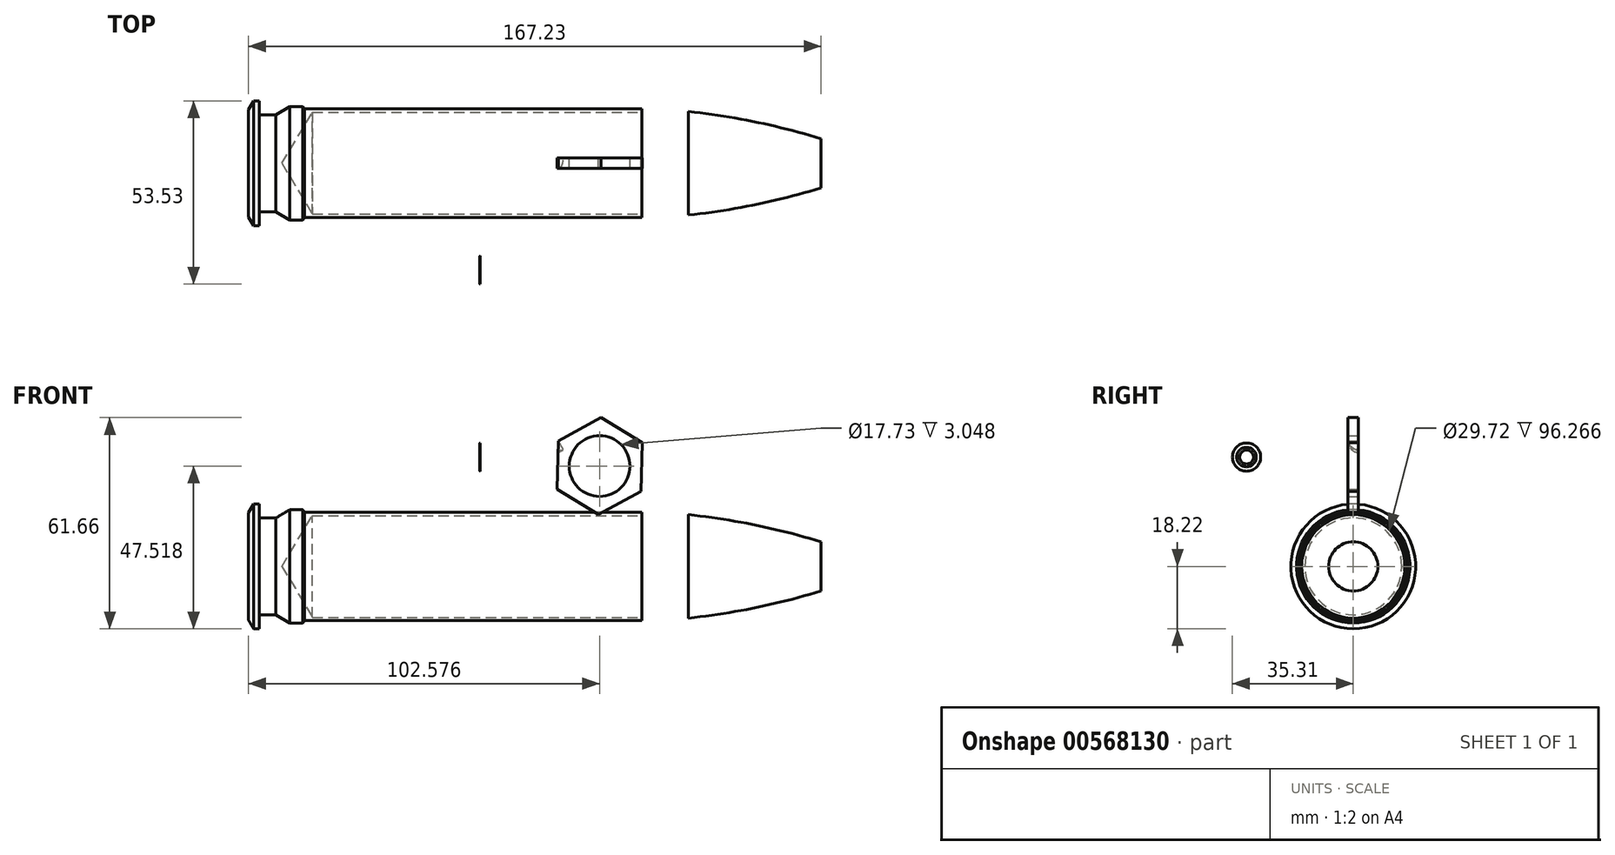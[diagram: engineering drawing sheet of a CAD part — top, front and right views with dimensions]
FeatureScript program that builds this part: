
annotation { "Feature Type Name" : "Feature", "Feature Type Description" : "" }
export const myFeature = defineFeature(function(context is Context, id is Id, definition is map)
    precondition{}
    {
        {
            var Q0;
            Q0=qCreatedBy(makeId("Front.planeOp"),FACE);
            var sketch = newSketch(context, id + "F0", { "sketchPlane" : qUnion([Q0])});
            skLineSegment(sketch, "E0", {"start": v(-51.8, -16.56) * mm, "end": v(-51.19, -15.92) * mm});
            skLineSegment(sketch, "E1", {"start": v(-51.19, -15.92) * mm, "end": v(47.36, -15.92) * mm});
            skLineSegment(sketch, "E2", {"start": v(-51.19, 15.87) * mm, "end": v(-51.75, 16.55) * mm});
            skLineSegment(sketch, "E3", {"start": v(-55.62, -16.56) * mm, "end": v(-59.6, -14.07) * mm});
            skLineSegment(sketch, "E4", {"start": v(-55.56, 16.55) * mm, "end": v(-59.6, 14.15) * mm});
            skLineSegment(sketch, "E5", {"start": v(-59.6, 14.15) * mm, "end": v(-64.43, 14.15) * mm});
            skLineSegment(sketch, "E6", {"start": v(-59.6, -14.07) * mm, "end": v(-64.43, -14.07) * mm});
            skLineSegment(sketch, "E7", {"start": v(-64.43, -14.07) * mm, "end": v(-64.43, -18.14) * mm});
            skLineSegment(sketch, "E8", {"start": v(-64.43, -18.14) * mm, "end": v(-67.6, -18.14) * mm});
            skLineSegment(sketch, "E9", {"start": v(-64.43, 14.15) * mm, "end": v(-64.43, 18.22) * mm});
            skLineSegment(sketch, "E10", {"start": v(-64.43, 18.22) * mm, "end": v(-67.6, 18.22) * mm});
            skLineSegment(sketch, "E11", {"start": v(-67.6, 18.22) * mm, "end": v(-67.6, -18.14) * mm});
            skLineSegment(sketch, "E12", {"start": v(-51.8, -16.56) * mm, "end": v(-55.62, -16.56) * mm});
            skLineSegment(sketch, "E13", {"start": v(-55.56, 16.55) * mm, "end": v(-51.75, 16.55) * mm});
            skLineSegment(sketch, "E14", {"start": v(-51.19, 15.87) * mm, "end": v(47.36, 15.87) * mm});
            skLineSegment(sketch, "E15", {"start": v(47.36, 15.87) * mm, "end": v(47.36, -15.92) * mm});
            skLineSegment(sketch, "E16", {"start": v(-67.6, 0) * mm, "end": v(47.36, 0) * mm});
            skSolve(sketch);
        }
        {
            var Q0;
            Q0=makeQuery(id+"F0.imprint","IMPRINT",FACE,{"disambiguationData":[TD([[makeQuery(id+"F0.imprint","IMPRINT",EDGE,{"derivedFrom":sQuery(id+"F0.wireOp",EDGE,"E2")}),1.0]])]});
            var Q1;
            Q1=sQuery(id+"F0.wireOp",EDGE,"E16");
            revolve(context, id + "F1", {"entities" : qUnion([Q0]), "axis" : qUnion([Q1]), "revolveType" : RevolveType.FULL});
        }
        {
            var Q0;
            Q0=makeQuery(id+"F1.opRevolve","SWEPT_EDGE",EDGE,{"disambiguationData":[OSD([sQuery(id+"F0.wireOp",EDGE,"E10"),sQuery(id+"F0.wireOp",EDGE,"E11")])]});
            chamfer(context, id + "F2", {"entities" : qUnion([Q0]), "chamferType" : ChamferType.OFFSET_ANGLE, "width" : 2.54 * mm, "oppositeDirection" : false, "angle" : 30 * degree, "tangentPropagation" : true});
        }
        {
            var Q0;
            Q0=makeQuery(id+"F1.opRevolve","SWEPT_FACE",FACE,{"disambiguationData":[OSD([sQuery(id+"F0.wireOp",EDGE,"E15")])]});
            cPlane(context, id + "F3", {"entities" : qUnion([Q0]), "cplaneType" : CPlaneType.OFFSET, "offset" : 0.25 * mm, "width" : 152.4 * mm, "height" : 152.4 * mm});
        }
        {
            var Q0;
            Q0=qCreatedBy(id+"F3.planeOp",FACE);
            var sketch = newSketch(context, id + "F4", { "sketchPlane" : qUnion([Q0])});
            skCircle(sketch, "E17", {"center": v(0, 0) * mm, "radius": 14.86 * mm});
            skSolve(sketch);
        }
        {
            var Q0;
            Q0=sQuery(id+"F4.wireOp",VERTEX,"E17.center");
            var Q1;
            Q1=makeQuery(id+"F1.opRevolve","SWEPT_BODY",BODY,{"disambiguationData":[OSD([sQuery(id+"F0.wireOp",EDGE,"E2"),sQuery(id+"F0.wireOp",EDGE,"E4"),sQuery(id+"F0.wireOp",EDGE,"E5"),sQuery(id+"F0.wireOp",EDGE,"E9"),sQuery(id+"F0.wireOp",EDGE,"E10"),sQuery(id+"F0.wireOp",EDGE,"E11"),sQuery(id+"F0.wireOp",EDGE,"E13"),sQuery(id+"F0.wireOp",EDGE,"E14"),sQuery(id+"F0.wireOp",EDGE,"E15"),sQuery(id+"F0.wireOp",EDGE,"E16")])]});
            hole(context, id + "F5", {"style" : HoleStyle.SIMPLE, "endStyle" : HoleEndStyle.BLIND, "holeDiameter" : 29.72 * mm, "holeDepth" : 96.52 * mm, "isTappedThrough" : true, "tappedDepth" : 12.7 * mm, "tapClearance" : 3, "startFromSketch" : true, "locations" : qUnion([Q0]), "scope" : qUnion([Q1])});
        }
        {
            var Q0;
            Q0=qCreatedBy(makeId("Right.planeOp"),FACE);
            var sketch = newSketch(context, id + "F6", { "sketchPlane" : qUnion([Q0])});
            skCircle(sketch, "E18", {"center": v(-31.18, 31.94) * mm, "radius": 4.13 * mm});
            skCircle(sketch, "E19", {"center": v(-31.18, 31.94) * mm, "radius": 2.86 * mm});
            skCircle(sketch, "E20", {"center": v(-31.18, 31.94) * mm, "radius": 2.03 * mm});
            skSolve(sketch);
        }
        {
            var Q0;
            Q0=makeQuery(id+"F6.imprint","IMPRINT",FACE,{"disambiguationData":[TD([[makeQuery(id+"F6.imprint","IMPRINT",EDGE,{"derivedFrom":sQuery(id+"F6.wireOp",EDGE,"E18")}),1.0]])]});
            var Q1;
            Q1=makeQuery(id+"F6.imprint","IMPRINT",FACE,{"disambiguationData":[TD([[makeQuery(id+"F6.imprint","IMPRINT",EDGE,{"derivedFrom":sQuery(id+"F6.wireOp",EDGE,"E20")}),1.0]])]});
            extrude(context, id + "F7", {"entities" : qUnion([Q0, Q1]), "endBound" : BoundingType.SYMMETRIC, "oppositeDirection" : true, "depth" : 0.2 * mm, "offsetDistance" : 25.4 * mm});
        }
        {
            var Q0;
            Q0=makeQuery(id+"F7.opExtrude","CAP_EDGE",EDGE,{"disambiguationData":[OSD([sQuery(id+"F6.wireOp",EDGE,"E18")])],"isStart":false});
            var Q1;
            Q1=makeQuery(id+"F7.opExtrude","CAP_EDGE",EDGE,{"disambiguationData":[OSD([sQuery(id+"F6.wireOp",EDGE,"E19")])],"isStart":false});
            fillet(context, id + "F8", {"entities" : qUnion([Q0, Q1]), "radius" : 0.2 * mm, "tangentPropagation" : true, "allowEdgeOverflow" : false});
        }
        {
            var Q0;
            Q0=makeQuery(id+"F7.opExtrude","CAP_EDGE",EDGE,{"disambiguationData":[OSD([sQuery(id+"F6.wireOp",EDGE,"E20")])],"isStart":false});
            fillet(context, id + "F9", {"entities" : qUnion([Q0]), "radius" : 1.17 * mm, "tangentPropagation" : true, "rho" : 0.5, "crossSection" : FilletCrossSection.CONIC, "allowEdgeOverflow" : false});
        }
        {
            var Q0;
            Q0=qCreatedBy(makeId("Front.planeOp"),FACE);
            var sketch = newSketch(context, id + "F10", { "sketchPlane" : qUnion([Q0])});
            skLineSegment(sketch, "E21", {"start": v(60.9, 14.72) * mm, "end": v(60.9, -15.12) * mm});
            skLineSegment(sketch, "E22", {"start": v(99.62, 5.52) * mm, "end": v(99.62, -7.18) * mm});
            skArc(sketch, "E23", {"start": v(99.62, 5.52) * mm, "mid": v(80.48, 11.05) * mm, "end": v(60.9, 14.72) * mm});
            skArc(sketch, "E24", {"start": v(60.9, -15.12) * mm, "mid": v(80.45, -12.07) * mm, "end": v(99.62, -7.18) * mm});
            skLineSegment(sketch, "E25", {"start": v(60.9, 0) * mm, "end": v(99.62, 0) * mm});
            skSolve(sketch);
        }
        {
            var Q0;
            {var subQ0=sQuery(id+"F10.wireOp",EDGE,"E24");Q0=makeQuery(id+"F10.imprint","IMPRINT",FACE,{"disambiguationData":[TD([[makeQuery(id+"F10.imprint","IMPRINT",EDGE,{"derivedFrom":subQ0}),1.0]])]});}
            var Q1;
            Q1=sQuery(id+"F10.wireOp",EDGE,"E25");
            revolve(context, id + "F11", {"entities" : qUnion([Q0]), "axis" : qUnion([Q1]), "revolveType" : RevolveType.FULL});
        }
        {
            var Q0;
            Q0=qCreatedBy(makeId("Front.planeOp"),FACE);
            var sketch = newSketch(context, id + "F12", { "sketchPlane" : qUnion([Q0])});
            skCircle(sketch, "E26.cCircle", {"center": v(34.97, 29.3) * mm, "radius": 12.25 * mm, "construction": true});
            skLineSegment(sketch, "E26.0", {"start": v(22.89, 36.67) * mm, "end": v(35.31, 43.44) * mm});
            skLineSegment(sketch, "E26.1", {"start": v(35.31, 43.44) * mm, "end": v(47.39, 36.07) * mm});
            skLineSegment(sketch, "E26.2", {"start": v(47.39, 36.07) * mm, "end": v(47.04, 21.92) * mm});
            skLineSegment(sketch, "E26.3", {"start": v(47.04, 21.92) * mm, "end": v(34.62, 15.15) * mm});
            skLineSegment(sketch, "E26.4", {"start": v(34.62, 15.15) * mm, "end": v(22.54, 22.53) * mm});
            skLineSegment(sketch, "E26.5", {"start": v(22.54, 22.53) * mm, "end": v(22.89, 36.67) * mm});
            skPoint(sketch, "E26.0.midPoint", {"position": v(29.1, 40.06) * mm});
            skCircle(sketch, "E27", {"center": v(34.97, 29.3) * mm, "radius": 8.86 * mm});
            skSolve(sketch);
        }
        {
            var Q0;
            Q0 = qSketchRegion(id + "F12", true);
            extrude(context, id + "F13", {"entities" : qUnion([Q0]), "endBound" : BoundingType.SYMMETRIC, "depth" : 3.05 * mm, "offsetDistance" : 25.4 * mm});
        }
        {
            var Q0;
            Q0 = qSketchRegion(id + "F12", true);
            extrude(context, id + "F14", {"entities" : qUnion([Q0]), "depth" : 3.05 * mm, "offsetDistance" : 25.4 * mm});
        }
        {
            var Q0;
            Q0=makeQuery(id+"F14.opExtrude","SWEPT_BODY",BODY,{"disambiguationData":[OSD([sQuery(id+"F12.wireOp",EDGE,"E26.0"),sQuery(id+"F12.wireOp",EDGE,"E26.1"),sQuery(id+"F12.wireOp",EDGE,"E26.2"),sQuery(id+"F12.wireOp",EDGE,"E26.3"),sQuery(id+"F12.wireOp",EDGE,"E26.4"),sQuery(id+"F12.wireOp",EDGE,"E26.5"),sQuery(id+"F12.wireOp",EDGE,"E27")])]});
            deleteBodies(context, id + "F15", {"entities" : qUnion([Q0])});
        }
        {
            var Q0;
            Q0=makeQuery(id+"F13.opExtrude","SWEPT_FACE",FACE,{"disambiguationData":[OSD([sQuery(id+"F12.wireOp",EDGE,"E26.0")])]});
            var sketch = newSketch(context, id + "F16", { "sketchPlane" : qUnion([Q0])});
            skLineSegment(sketch, "E28", {"start": v(51.8, -1.52) * mm, "end": v(51.8, 1.52) * mm, "construction": true});
            skLineSegment(sketch, "E29", {"start": v(51.8, 1.52) * mm, "end": v(51.8, 0) * mm, "construction": true});
            skLineSegment(sketch, "E30", {"start": v(51.8, 0) * mm, "end": v(37.65, 0) * mm, "construction": true});
            skLineSegment(sketch, "E31", {"start": v(37.65, -1.52) * mm, "end": v(35.48, -0.4) * mm});
            skLineSegment(sketch, "E32", {"start": v(35.48, -0.4) * mm, "end": v(35.48, -1.52) * mm});
            skLineSegment(sketch, "E33", {"start": v(35.48, -1.52) * mm, "end": v(37.65, -1.52) * mm});
            skLineSegment(sketch, "E34.MirrorCS", {"start": v(35.48, 1.52) * mm, "end": v(37.65, 1.52) * mm});
            skLineSegment(sketch, "E35.MirrorCS", {"start": v(37.65, 1.52) * mm, "end": v(35.48, 0.4) * mm});
            skLineSegment(sketch, "E36.MirrorCS", {"start": v(35.48, 0.4) * mm, "end": v(35.48, 1.52) * mm});
            skSolve(sketch);
        }
        {
            var Q0;
            Q0 = qSketchRegion(id + "F16", true);
            var Q1;
            Q1=sQuery(id+"F16.wireOp",EDGE,"E32");
            var Q2;
            Q2=sQuery(id+"F16.wireOp",EDGE,"E33");
            var Q3;
            Q3=sQuery(id+"F16.wireOp",EDGE,"E31");
            var Q4;
            Q4=sQuery(id+"F16.wireOp",EDGE,"E35.MirrorCS");
            var Q5;
            Q5=sQuery(id+"F16.wireOp",EDGE,"E34.MirrorCS");
            var Q6;
            Q6=sQuery(id+"F16.wireOp",EDGE,"E36.MirrorCS");
            var Q7;
            Q7=makeQuery(id+"F13.opExtrude","CAP_EDGE",EDGE,{"disambiguationData":[OSD([sQuery(id+"F12.wireOp",EDGE,"E26.0")])],"isStart":true});
            revolve(context, id + "F17", {"operationType" : NewBodyOperationType.REMOVE, "entities" : qUnion([Q0]), "surfaceEntities" : qUnion([Q1, Q2, Q3, Q4, Q5, Q6]), "axis" : qUnion([Q7]), "revolveType" : RevolveType.FULL, "oppositeDirection" : true});
        }
    });
